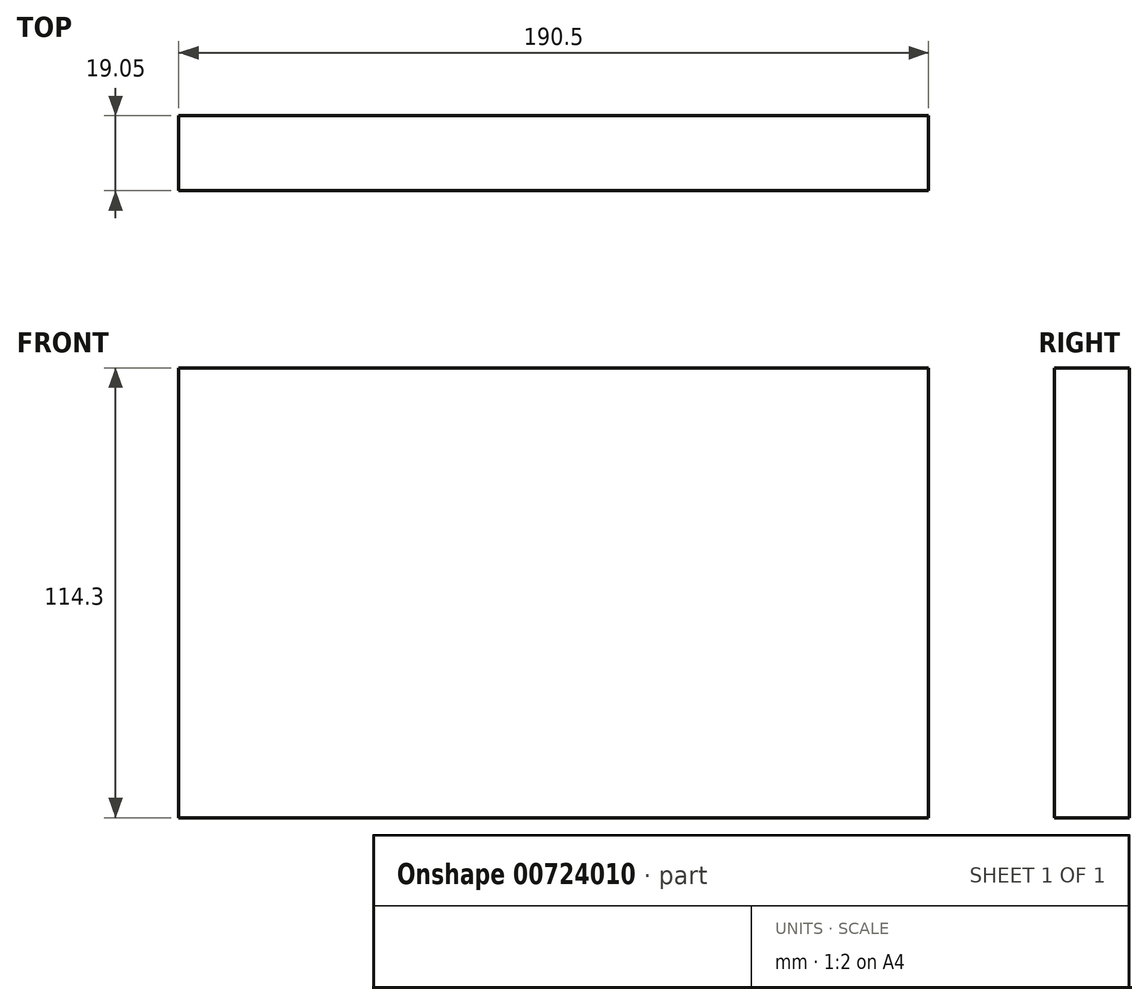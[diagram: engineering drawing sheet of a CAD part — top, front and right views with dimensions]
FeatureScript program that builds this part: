
annotation { "Feature Type Name" : "Feature", "Feature Type Description" : "" }
export const myFeature = defineFeature(function(context is Context, id is Id, definition is map)
    precondition{}
    {
        {
            var Q0;
            Q0=qCreatedBy(makeId("Front.planeOp"),FACE);
            var sketch = newSketch(context, id + "F0", { "sketchPlane" : qUnion([Q0])});
            skLineSegment(sketch, "E0.bottom", {"start": v(0, 0) * mm, "end": v(190.5, 0) * mm});
            skLineSegment(sketch, "E0.top", {"start": v(0, 114.3) * mm, "end": v(190.5, 114.3) * mm});
            skLineSegment(sketch, "E0.left", {"start": v(0, 0) * mm, "end": v(0, 114.3) * mm});
            skLineSegment(sketch, "E0.right", {"start": v(190.5, 0) * mm, "end": v(190.5, 114.3) * mm});
            skSolve(sketch);
        }
        {
            var Q0;
            Q0=makeQuery(id+"F0.imprint","IMPRINT",FACE,{"disambiguationData":[TD([[makeQuery(id+"F0.imprint","IMPRINT",EDGE,{"derivedFrom":sQuery(id+"F0.wireOp",EDGE,"E0.bottom")}),1.0]])]});
            extrude(context, id + "F1", {"entities" : qUnion([Q0]), "depth" : 19.05 * mm, "offsetDistance" : 25.4 * mm});
        }
    });
